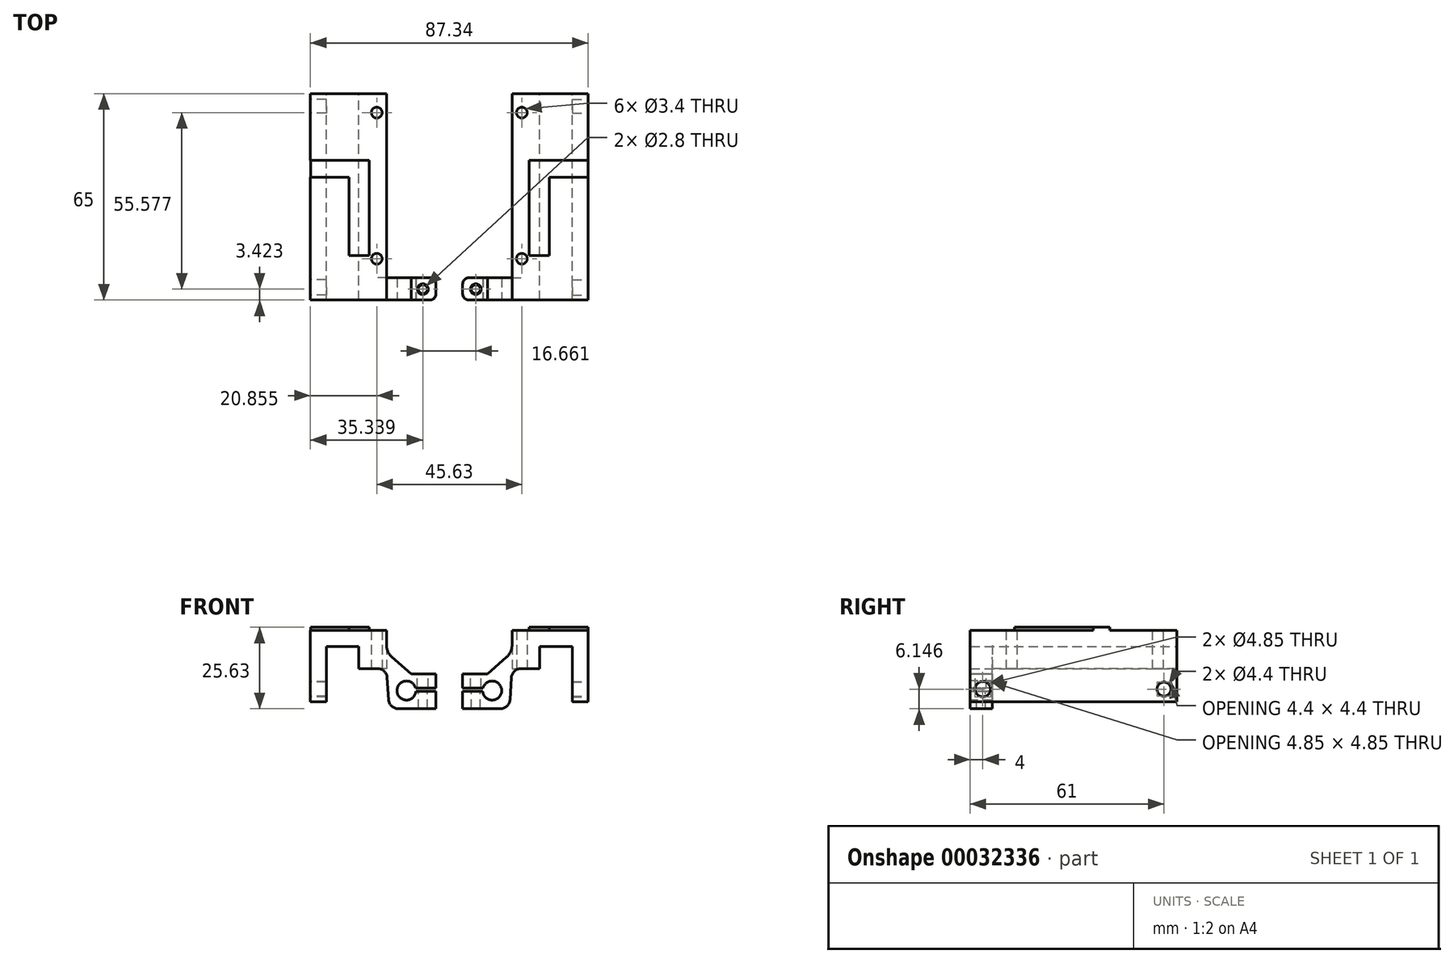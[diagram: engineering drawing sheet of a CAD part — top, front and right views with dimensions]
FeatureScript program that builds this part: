
annotation { "Feature Type Name" : "Feature", "Feature Type Description" : "" }
export const myFeature = defineFeature(function(context is Context, id is Id, definition is map)
    precondition{}
    {
        {
            var Q0;
            Q0=qCreatedBy(makeId("Front.planeOp"),FACE);
            var sketch = newSketch(context, id + "F0", { "sketchPlane" : qUnion([Q0])});
            skLineSegment(sketch, "E0", {"start": v(-18.67, 7.33) * mm, "end": v(-18.67, 29.8) * mm});
            skLineSegment(sketch, "E1", {"start": v(-18.67, 29.8) * mm, "end": v(5.26, 29.8) * mm});
            skLineSegment(sketch, "E2", {"start": v(5.26, 29.8) * mm, "end": v(5.26, 22.94) * mm});
            skLineSegment(sketch, "E3", {"start": v(-3.47, 17.8) * mm, "end": v(-3.47, 24.8) * mm});
            skLineSegment(sketch, "E4", {"start": v(-3.47, 24.8) * mm, "end": v(-13.67, 24.8) * mm});
            skLineSegment(sketch, "E5", {"start": v(-13.67, 24.8) * mm, "end": v(-13.67, 7.33) * mm});
            skLineSegment(sketch, "E6", {"start": v(-13.67, 7.33) * mm, "end": v(-18.67, 7.33) * mm});
            skLineSegment(sketch, "E7", {"start": v(5.26, 22.94) * mm, "end": v(5.26, 17.8) * mm});
            skLineSegment(sketch, "E8", {"start": v(5.26, 17.8) * mm, "end": v(-3.47, 17.8) * mm});
            skLineSegment(sketch, "E9", {"start": v(5.26, 22.94) * mm, "end": v(5.26, 22.94) * mm});
            skLineSegment(sketch, "E10", {"start": v(20.79, 16.13) * mm, "end": v(20.79, 11.7) * mm});
            skLineSegment(sketch, "E11", {"start": v(20.79, 11.7) * mm, "end": v(13.49, 11.7) * mm});
            skLineSegment(sketch, "E12", {"start": v(13.49, 11.7) * mm, "end": v(13.49, 10.67) * mm});
            skLineSegment(sketch, "E13", {"start": v(13.49, 10.67) * mm, "end": v(20.82, 10.67) * mm});
            skLineSegment(sketch, "E14", {"start": v(20.82, 10.67) * mm, "end": v(20.82, 5.18) * mm});
            skLineSegment(sketch, "E15", {"start": v(20.82, 5.18) * mm, "end": v(6.11, 5.18) * mm});
            skLineSegment(sketch, "E16", {"start": v(6.11, 5.18) * mm, "end": v(5.26, 17.8) * mm});
            skLineSegment(sketch, "E17", {"start": v(20.79, 16.13) * mm, "end": v(13, 16.13) * mm});
            skLineSegment(sketch, "E18", {"start": v(13, 16.13) * mm, "end": v(5.26, 22.94) * mm});
            skLineSegment(sketch, "E19", {"start": v(-3.47, 17.8) * mm, "end": v(-3.47, 5.18) * mm});
            skLineSegment(sketch, "E20", {"start": v(-3.47, 5.18) * mm, "end": v(6.11, 5.18) * mm});
            skSolve(sketch);
        }
        {
            var Q0;
            Q0=makeQuery(id+"F0.imprint","IMPRINT",FACE,{"disambiguationData":[TD([[makeQuery(id+"F0.imprint","IMPRINT",EDGE,{"derivedFrom":sQuery(id+"F0.wireOp",EDGE,"E0")}),-1.0]])]});
            var Q1;
            {var subQ2=sQuery(id+"F0.wireOp",EDGE,"69cbcc5d-e0c3-48db-8baf-3487a8abab7d");Q1=makeQuery(id+"F0.imprint","IMPRINT",FACE,{"disambiguationData":[TD([[makeQuery(id+"F0.imprint","IMPRINT",EDGE,{"derivedFrom":subQ2}),-1.0]])]});}
            var Q2;
            Q2=makeQuery(id+"F0.imprint","IMPRINT",FACE,{"disambiguationData":[TD([[makeQuery(id+"F0.imprint","IMPRINT",EDGE,{"derivedFrom":sQuery(id+"F0.wireOp",EDGE,"E7")}),1.0]])]});
            extrude(context, id + "F1", {"entities" : qUnion([Q0, Q1, Q2]), "depth" : 7 * mm});
        }
        {
            var Q0;
            Q0=makeQuery(id+"F0.imprint","IMPRINT",FACE,{"disambiguationData":[TD([[makeQuery(id+"F0.imprint","IMPRINT",EDGE,{"derivedFrom":sQuery(id+"F0.wireOp",EDGE,"E0")}),-1.0]])]});
            extrude(context, id + "F2", {"entities" : qUnion([Q0]), "operationType" : NewBodyOperationType.ADD, "oppositeDirection" : true, "depth" : 58 * mm});
        }
        {
            var Q0;
            {var subQ0=sQuery(id+"F0.wireOp",EDGE,"E8");Q0=makeQuery(id+"F2.boolean.opBoolean","MERGE",FACE,{"derivedFrom":[makeQuery(id+"F1.opExtrude","SWEPT_FACE",FACE,{"disambiguationData":[OSD([subQ0])]}),makeQuery(id+"F2.opExtrude","SWEPT_FACE",FACE,{"disambiguationData":[OSD([subQ0])]})]});}
            var sketch = newSketch(context, id + "F3", { "sketchPlane" : qUnion([Q0])});
            skCircle(sketch, "E21", {"center": v(2.19, -6) * mm, "radius": 1.7 * mm});
            skCircle(sketch, "E22", {"center": v(2.19, -52) * mm, "radius": 1.7 * mm});
            skCircle(sketch, "E23", {"center": v(17.69, -29) * mm, "radius": 11 * mm});
            skSolve(sketch);
        }
        {
            var Q0;
            Q0=qSketchRegion(id+"F3",true);
            extrude(context, id + "F4", {"entities" : qUnion([Q0]), "operationType" : NewBodyOperationType.REMOVE, "endBound" : BoundingType.THROUGH_ALL, "oppositeDirection" : true, "depth" : 25 * mm});
        }
        {
            var Q0;
            Q0=makeQuery(id+"F1.opExtrude","CAP_FACE",FACE,{"disambiguationData":[OSD([sQuery(id+"F0.wireOp",EDGE,"E0"),sQuery(id+"F0.wireOp",EDGE,"E1"),sQuery(id+"F0.wireOp",EDGE,"E2"),sQuery(id+"F0.wireOp",EDGE,"E3"),sQuery(id+"F0.wireOp",EDGE,"E4"),sQuery(id+"F0.wireOp",EDGE,"E5"),sQuery(id+"F0.wireOp",EDGE,"E6"),sQuery(id+"F0.wireOp",EDGE,"E8"),sQuery(id+"F0.wireOp",EDGE,"E9"),sQuery(id+"F0.wireOp",EDGE,"58f11638-63e7-4b32-8aff-a1ba3c53649b"),sQuery(id+"F0.wireOp",EDGE,"E10"),sQuery(id+"F0.wireOp",EDGE,"E11"),sQuery(id+"F0.wireOp",EDGE,"E12"),sQuery(id+"F0.wireOp",EDGE,"E13"),sQuery(id+"F0.wireOp",EDGE,"E14"),sQuery(id+"F0.wireOp",EDGE,"E15"),sQuery(id+"F0.wireOp",EDGE,"E16")])],"isStart":false});
            var sketch = newSketch(context, id + "F5", { "sketchPlane" : qUnion([Q0])});
            skCircle(sketch, "E24", {"center": v(11.53, 10.9) * mm, "radius": 3 * mm});
            skSolve(sketch);
        }
        {
            var Q0;
            Q0=qSketchRegion(id+"F5",true);
            extrude(context, id + "F6", {"entities" : qUnion([Q0]), "operationType" : NewBodyOperationType.REMOVE, "oppositeDirection" : true, "depth" : 10 * mm});
        }
        {
            var Q0;
            Q0=qSketchRegion(id+"F3",true);
            extrude(context, id + "F7", {"entities" : qUnion([Q0]), "operationType" : NewBodyOperationType.REMOVE, "endBound" : BoundingType.THROUGH_ALL, "oppositeDirection" : true, "depth" : 25 * mm});
        }
        {
            var Q0;
            Q0=makeQuery(id+"F1.opExtrude","SWEPT_FACE",FACE,{"disambiguationData":[OSD([sQuery(id+"F0.wireOp",EDGE,"E17")])]});
            var sketch = newSketch(context, id + "F8", { "sketchPlane" : qUnion([Q0])});
            skCircle(sketch, "E25", {"center": v(16.67, -3.58) * mm, "radius": 1.7 * mm});
            skCircle(sketch, "E26", {"center": v(16.67, -3.58) * mm, "radius": 1.4 * mm});
            skSolve(sketch);
        }
        {
            var Q0;
            Q0=makeQuery(id+"F8.imprint","IMPRINT",FACE,{"disambiguationData":[TD([[makeQuery(id+"F8.imprint","IMPRINT",EDGE,{"derivedFrom":sQuery(id+"F8.wireOp",EDGE,"E26")}),1.0]])]});
            extrude(context, id + "F9", {"entities" : qUnion([Q0]), "operationType" : NewBodyOperationType.REMOVE, "endBound" : BoundingType.THROUGH_ALL, "oppositeDirection" : true, "depth" : 25 * mm});
        }
        {
            var Q0;
            Q0=makeQuery(id+"F8.imprint","IMPRINT",FACE,{"disambiguationData":[TD([[makeQuery(id+"F8.imprint","IMPRINT",EDGE,{"derivedFrom":sQuery(id+"F8.wireOp",EDGE,"E25")}),1.0]])]});
            extrude(context, id + "F10", {"entities" : qUnion([Q0]), "operationType" : NewBodyOperationType.REMOVE, "endBound" : BoundingType.UP_TO_NEXT, "oppositeDirection" : true, "depth" : 25 * mm});
        }
        {
            var Q0;
            Q0=makeQuery(id+"F1.opExtrude","SWEPT_EDGE",EDGE,{"disambiguationData":[OSD([sQuery(id+"F0.wireOp",EDGE,"E2"),sQuery(id+"F0.wireOp",EDGE,"E7"),sQuery(id+"F0.wireOp",EDGE,"E18")])]});
            fillet(context, id + "F11", {"entities" : qUnion([Q0]), "radius" : 5 * mm, "tangentPropagation" : true, "allowEdgeOverflow" : false});
        }
        {
            var Q0;
            Q0=makeQuery(id+"F1.opExtrude","SWEPT_EDGE",EDGE,{"disambiguationData":[OSD([sQuery(id+"F0.wireOp",EDGE,"E7"),sQuery(id+"F0.wireOp",EDGE,"E8"),sQuery(id+"F0.wireOp",EDGE,"E16")])]});
            fillet(context, id + "F12", {"entities" : qUnion([Q0]), "radius" : 3 * mm, "tangentPropagation" : true, "allowEdgeOverflow" : false});
        }
        {
            var Q0;
            Q0=makeQuery(id+"F1.opExtrude","SWEPT_EDGE",EDGE,{"disambiguationData":[OSD([sQuery(id+"F0.wireOp",EDGE,"E15"),sQuery(id+"F0.wireOp",EDGE,"E16")])]});
            fillet(context, id + "F13", {"entities" : qUnion([Q0]), "radius" : 3 * mm, "tangentPropagation" : true, "allowEdgeOverflow" : false});
        }
        {
            var Q0;
            Q0=makeQuery(id+"F1.opExtrude","CAP_EDGE",EDGE,{"disambiguationData":[OSD([sQuery(id+"F0.wireOp",EDGE,"E10")])],"isStart":false});
            var Q1;
            Q1=makeQuery(id+"F1.opExtrude","CAP_EDGE",EDGE,{"disambiguationData":[OSD([sQuery(id+"F0.wireOp",EDGE,"E14")])],"isStart":false});
            var Q2;
            Q2=makeQuery(id+"F1.opExtrude","CAP_EDGE",EDGE,{"disambiguationData":[OSD([sQuery(id+"F0.wireOp",EDGE,"E10")])],"isStart":true});
            var Q3;
            Q3=makeQuery(id+"F1.opExtrude","CAP_EDGE",EDGE,{"disambiguationData":[OSD([sQuery(id+"F0.wireOp",EDGE,"E14")])],"isStart":true});
            fillet(context, id + "F14", {"entities" : qUnion([Q0, Q1, Q2, Q3]), "radius" : 2 * mm, "tangentPropagation" : true, "allowEdgeOverflow" : false});
        }
        {
            var Q0;
            {var subQ0=sQuery(id+"F0.wireOp",EDGE,"E0");Q0=makeQuery(id+"F2.boolean.opBoolean","MERGE",FACE,{"derivedFrom":[makeQuery(id+"F1.opExtrude","SWEPT_FACE",FACE,{"disambiguationData":[OSD([subQ0])]}),makeQuery(id+"F2.opExtrude","SWEPT_FACE",FACE,{"disambiguationData":[OSD([subQ0])]})]});}
            var sketch = newSketch(context, id + "F15", { "sketchPlane" : qUnion([Q0])});
            skCircle(sketch, "E27", {"center": v(-54, 11.33) * mm, "radius": 2.2 * mm});
            skCircle(sketch, "E28", {"center": v(3, 11.33) * mm, "radius": 2.43 * mm});
            skSolve(sketch);
        }
        {
            var Q0;
            Q0=qSketchRegion(id+"F15",true);
            extrude(context, id + "F16", {"entities" : qUnion([Q0]), "operationType" : NewBodyOperationType.REMOVE, "oppositeDirection" : true, "depth" : 6 * mm});
        }
        {
            var Q0;
            {var subQ0=sQuery(id+"F0.wireOp",EDGE,"E1");Q0=makeQuery(id+"F2.boolean.opBoolean","MERGE",FACE,{"derivedFrom":[makeQuery(id+"F1.opExtrude","SWEPT_FACE",FACE,{"disambiguationData":[OSD([subQ0])]}),makeQuery(id+"F2.opExtrude","SWEPT_FACE",FACE,{"disambiguationData":[OSD([subQ0])]})]});}
            var sketch = newSketch(context, id + "F17", { "sketchPlane" : qUnion([Q0])});
            skText(sketch, "E29", { "text": "L", "fontName": "OpenSans-Bold.ttf"});
            const initialGuessF17  = {"E29": [0.0036, 0.03693, -1, 0, 0.0302]};
            skSetInitialGuess(sketch, initialGuessF17);
            skSolve(sketch);
        }
        {
            var Q0;
            Q0=qSketchRegion(id+"F17",true);
            extrude(context, id + "F18", {"entities" : qUnion([Q0]), "operationType" : NewBodyOperationType.ADD, "depth" : 1 * mm});
        }
        {
            var Q0;
            Q0=makeQuery(id+"F1.opExtrude","SWEPT_BODY",BODY,{"disambiguationData":[OSD([sQuery(id+"F0.wireOp",EDGE,"E0"),sQuery(id+"F0.wireOp",EDGE,"E1"),sQuery(id+"F0.wireOp",EDGE,"E2"),sQuery(id+"F0.wireOp",EDGE,"E3"),sQuery(id+"F0.wireOp",EDGE,"E4"),sQuery(id+"F0.wireOp",EDGE,"E5"),sQuery(id+"F0.wireOp",EDGE,"E6"),sQuery(id+"F0.wireOp",EDGE,"E8"),sQuery(id+"F0.wireOp",EDGE,"E10"),sQuery(id+"F0.wireOp",EDGE,"E11"),sQuery(id+"F0.wireOp",EDGE,"E12"),sQuery(id+"F0.wireOp",EDGE,"E13"),sQuery(id+"F0.wireOp",EDGE,"E14"),sQuery(id+"F0.wireOp",EDGE,"E15"),sQuery(id+"F0.wireOp",EDGE,"E16"),sQuery(id+"F0.wireOp",EDGE,"E17"),sQuery(id+"F0.wireOp",EDGE,"E18")])]});
            var Q1;
            Q1=qCreatedBy(makeId("Right.planeOp"),FACE);
            mirror(context, id + "F19", {"entities" : qUnion([Q0]), "mirrorPlane" : qUnion([Q1])});
        }
        {
            var Q0;
            Q0=makeQuery(id+"F19.opPattern","COPY",BODY,{"derivedFrom":makeQuery(id+"F1.opExtrude","SWEPT_BODY",BODY,{"disambiguationData":[OSD([sQuery(id+"F0.wireOp",EDGE,"E0"),sQuery(id+"F0.wireOp",EDGE,"E1"),sQuery(id+"F0.wireOp",EDGE,"E2"),sQuery(id+"F0.wireOp",EDGE,"E3"),sQuery(id+"F0.wireOp",EDGE,"E4"),sQuery(id+"F0.wireOp",EDGE,"E5"),sQuery(id+"F0.wireOp",EDGE,"E6"),sQuery(id+"F0.wireOp",EDGE,"E8"),sQuery(id+"F0.wireOp",EDGE,"E10"),sQuery(id+"F0.wireOp",EDGE,"E11"),sQuery(id+"F0.wireOp",EDGE,"E12"),sQuery(id+"F0.wireOp",EDGE,"E13"),sQuery(id+"F0.wireOp",EDGE,"E14"),sQuery(id+"F0.wireOp",EDGE,"E15"),sQuery(id+"F0.wireOp",EDGE,"E16"),sQuery(id+"F0.wireOp",EDGE,"E17"),sQuery(id+"F0.wireOp",EDGE,"E18")])]}),"instanceName":"1"});
            transform(context, id + "F20", {"entities" : qUnion([Q0]), "transformType" : TransformType.TRANSLATION_3D, "dx" : 50 * mm, "dy" : 0 * mm, "dz" : 0 * mm, "makeCopy" : false});
        }
    });
